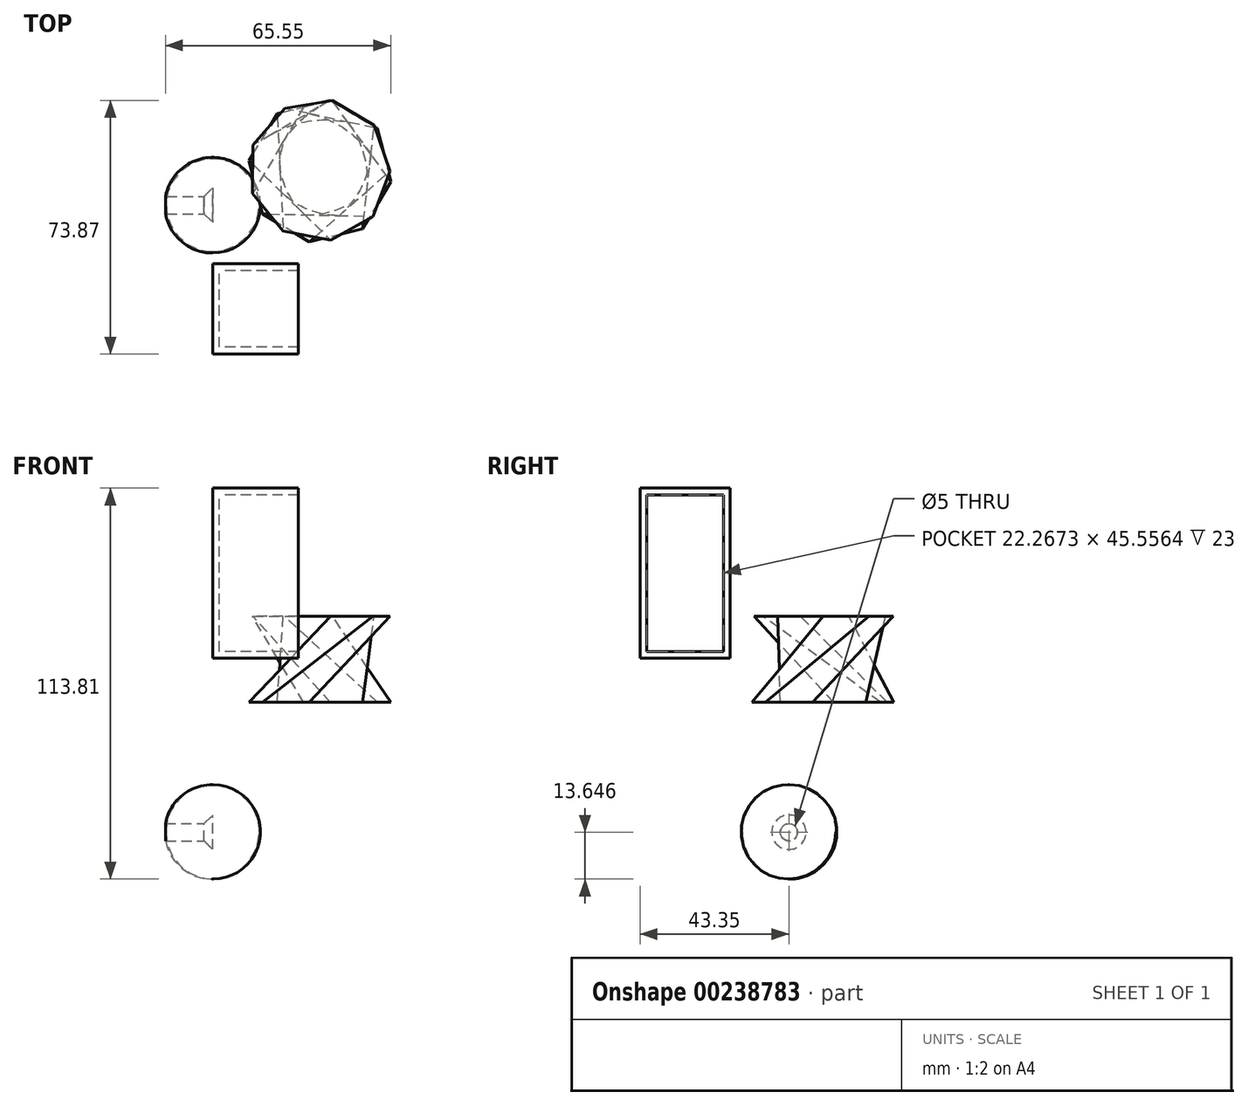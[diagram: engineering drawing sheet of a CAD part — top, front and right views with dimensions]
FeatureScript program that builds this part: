
annotation { "Feature Type Name" : "Feature", "Feature Type Description" : "" }
export const myFeature = defineFeature(function(context is Context, id is Id, definition is map)
    precondition{}
    {
        {
            var Q0;
            Q0=qCreatedBy(makeId("Top.planeOp"),FACE);
            cPlane(context, id + "F0", {"entities" : qUnion([Q0]), "cplaneType" : CPlaneType.OFFSET, "offset" : 25 * mm, "width" : 150 * mm, "height" : 150 * mm});
        }
        {
            var Q0;
            Q0=qCreatedBy(makeId("Top.planeOp"),FACE);
            var sketch = newSketch(context, id + "F1", { "sketchPlane" : qUnion([Q0])});
            skCircle(sketch, "E0.cCircle", {"center": v(31.22, 9.9) * mm, "radius": 19.26 * mm, "construction": true});
            skLineSegment(sketch, "E0.0", {"start": v(51.84, 6.85) * mm, "end": v(43.65, -6.85) * mm});
            skLineSegment(sketch, "E0.1", {"start": v(43.65, -6.85) * mm, "end": v(28.17, -10.73) * mm});
            skLineSegment(sketch, "E0.2", {"start": v(28.17, -10.73) * mm, "end": v(14.48, -2.54) * mm});
            skLineSegment(sketch, "E0.3", {"start": v(14.48, -2.54) * mm, "end": v(10.6, 12.94) * mm});
            skLineSegment(sketch, "E0.4", {"start": v(10.6, 12.94) * mm, "end": v(18.8, 26.63) * mm});
            skLineSegment(sketch, "E0.5", {"start": v(18.8, 26.63) * mm, "end": v(34.27, 30.52) * mm});
            skLineSegment(sketch, "E0.6", {"start": v(34.27, 30.52) * mm, "end": v(47.96, 22.32) * mm});
            skLineSegment(sketch, "E0.7", {"start": v(47.96, 22.32) * mm, "end": v(51.84, 6.85) * mm});
            skPoint(sketch, "E0.0.midPoint", {"position": v(47.75, 0) * mm});
            skSolve(sketch);
        }
        {
            var Q0;
            Q0=qCreatedBy(id+"F0.planeOp",FACE);
            var sketch = newSketch(context, id + "F2", { "sketchPlane" : qUnion([Q0])});
            skCircle(sketch, "E1.cCircle", {"center": v(31.04, 10.16) * mm, "radius": 20.6 * mm, "construction": true});
            skLineSegment(sketch, "E1.0", {"start": v(46.65, -3.27) * mm, "end": v(34.36, -10.16) * mm});
            skLineSegment(sketch, "E1.1", {"start": v(34.36, -10.16) * mm, "end": v(20.52, -7.54) * mm});
            skLineSegment(sketch, "E1.2", {"start": v(20.52, -7.54) * mm, "end": v(11.6, 3.36) * mm});
            skLineSegment(sketch, "E1.3", {"start": v(11.6, 3.36) * mm, "end": v(11.78, 17.45) * mm});
            skLineSegment(sketch, "E1.4", {"start": v(11.78, 17.45) * mm, "end": v(20.96, 28.13) * mm});
            skLineSegment(sketch, "E1.5", {"start": v(20.96, 28.13) * mm, "end": v(34.87, 30.4) * mm});
            skLineSegment(sketch, "E1.6", {"start": v(34.87, 30.4) * mm, "end": v(46.98, 23.2) * mm});
            skLineSegment(sketch, "E1.7", {"start": v(46.98, 23.2) * mm, "end": v(51.63, 9.9) * mm});
            skLineSegment(sketch, "E1.8", {"start": v(51.63, 9.9) * mm, "end": v(46.65, -3.27) * mm});
            skSolve(sketch);
        }
        {
            var Q0;
            Q0=makeQuery(id+"F1.imprint","IMPRINT",FACE,{"disambiguationData":[TD([[makeQuery(id+"F1.imprint","IMPRINT",EDGE,{"derivedFrom":sQuery(id+"F1.wireOp",EDGE,"E0.0")}),-1.0]])]});
            var Q1;
            Q1=makeQuery(id+"F2.imprint","IMPRINT",FACE,{"disambiguationData":[TD([[makeQuery(id+"F2.imprint","IMPRINT",EDGE,{"derivedFrom":sQuery(id+"F2.wireOp",EDGE,"E1.0")}),-1.0]])]});
            var Q2;
            Q2=sQuery(id+"F1.wireOp",VERTEX,"E0.2.start");
            var Q3;
            Q3=sQuery(id+"F2.wireOp",VERTEX,"E1.7.end");
            loft(context, id + "F3", {"sheetProfilesArray" : [{ "sheetProfileEntities" : qUnion([Q0]) }, { "sheetProfileEntities" : qUnion([Q1]) }], "matchConnections" : true, "connections" : [{ "connectionEntities" : qUnion([Q2, Q3]), "connectionEdgeQueries" : qUnion([]), "connectionEdgeParameters" : [] }]});
        }
        {
            var Q0;
            Q0=qCreatedBy(makeId("Front.planeOp"),FACE);
            var sketch = newSketch(context, id + "F4", { "sketchPlane" : qUnion([Q0])});
            skLineSegment(sketch, "E2", {"start": v(0, -17.33) * mm, "end": v(0, -59.43) * mm});
            skArc(sketch, "E3", {"start": v(0, -51.47) * mm, "mid": v(13.93, -37.73) * mm, "end": v(0, -24) * mm});
            skSolve(sketch);
        }
        {
            var Q0;
            {var subQ0=sQuery(id+"F4.wireOp",EDGE,"E3");Q0=makeQuery(id+"F4.imprint","IMPRINT",FACE,{"disambiguationData":[TD([[makeQuery(id+"F4.imprint","IMPRINT",EDGE,{"derivedFrom":subQ0}),1.0]])]});}
            var Q1;
            Q1=sQuery(id+"F4.wireOp",EDGE,"E2");
            revolve(context, id + "F5", {"entities" : qUnion([Q0]), "axis" : qUnion([Q1]), "revolveType" : RevolveType.FULL});
        }
        {
            var Q0;
            Q0=qCreatedBy(makeId("Right.planeOp"),FACE);
            var sketch = newSketch(context, id + "F6", { "sketchPlane" : qUnion([Q0])});
            skCircle(sketch, "E4", {"center": v(0, -37.82) * mm, "radius": 3.23 * mm});
            skSolve(sketch);
        }
        {
            var Q0;
            Q0=sQuery(id+"F6.wireOp",VERTEX,"E4.center");
            var Q1;
            Q1=makeQuery(id+"F5.opRevolve","SWEPT_BODY",BODY,{"disambiguationData":[OSD([sQuery(id+"F4.wireOp",EDGE,"E2"),sQuery(id+"F4.wireOp",EDGE,"E3")])]});
            hole(context, id + "F7", {"style" : HoleStyle.C_SINK, "endStyle" : HoleEndStyle.THROUGH, "holeDiameter" : 5 * mm, "cSinkDiameter" : 10 * mm, "cSinkAngle" : 90 * degree, "locations" : qUnion([Q0]), "scope" : qUnion([Q1]), "isTappedThrough" : true});
        }
        {
            var Q0;
            Q0=qCreatedBy(makeId("Right.planeOp"),FACE);
            var sketch = newSketch(context, id + "F8", { "sketchPlane" : qUnion([Q0])});
            skLineSegment(sketch, "E5.bottom", {"start": v(-43.35, 12.79) * mm, "end": v(-17.08, 12.79) * mm});
            skLineSegment(sketch, "E5.top", {"start": v(-43.35, 62.34) * mm, "end": v(-17.08, 62.34) * mm});
            skLineSegment(sketch, "E5.left", {"start": v(-43.35, 12.79) * mm, "end": v(-43.35, 62.34) * mm});
            skLineSegment(sketch, "E5.right", {"start": v(-17.08, 12.79) * mm, "end": v(-17.08, 62.34) * mm});
            skSolve(sketch);
        }
        {
            var Q0;
            Q0=makeQuery(id+"F8.imprint","IMPRINT",FACE,{"disambiguationData":[TD([[makeQuery(id+"F8.imprint","IMPRINT",EDGE,{"derivedFrom":sQuery(id+"F8.wireOp",EDGE,"E5.bottom")}),1.0]])]});
            extrude(context, id + "F9", {"entities" : qUnion([Q0]), "depth" : 25 * mm});
        }
        {
            var Q0;
            Q0=makeQuery(id+"F9.opExtrude","CAP_FACE",FACE,{"disambiguationData":[OSD([sQuery(id+"F8.wireOp",EDGE,"E5.bottom"),sQuery(id+"F8.wireOp",EDGE,"E5.top"),sQuery(id+"F8.wireOp",EDGE,"E5.left"),sQuery(id+"F8.wireOp",EDGE,"E5.right")])],"isStart":false});
            shell(context, id + "F10", {"entities" : qUnion([Q0]), "thickness" : 2 * mm});
        }
        {
            var Q0;
            Q0=qCreatedBy(makeId("Right.planeOp"),FACE);
            cPlane(context, id + "F11", {"entities" : qUnion([Q0]), "cplaneType" : CPlaneType.OFFSET, "offset" : 25 * mm, "width" : 150 * mm, "height" : 150 * mm});
        }
        {
            var Q0;
            Q0=qCreatedBy(id+"F11.planeOp",FACE);
            var sketch = newSketch(context, id + "F12", { "sketchPlane" : qUnion([Q0])});
            skLineSegment(sketch, "E6.0", {"start": v(-19.08, 14.79) * mm, "end": v(-19.08, 60.34) * mm});
            skLineSegment(sketch, "E7.0", {"start": v(-41.35, 60.34) * mm, "end": v(-19.08, 60.34) * mm});
            skLineSegment(sketch, "E8.0", {"start": v(-41.35, 14.79) * mm, "end": v(-41.35, 60.34) * mm});
            skLineSegment(sketch, "E9.0", {"start": v(-41.35, 14.79) * mm, "end": v(-19.08, 14.79) * mm});
            skFitSpline(sketch, "E10", {"points": [v(-19.08, 60.34) * mm, v(-28.49, 46.33) * mm, v(-41.35, 44.06) * mm, v(-41.35, 43.97) * mm], "startDerivative": vector(-11.4, -33.67) * mm, "endDerivative": vector(1.33, -2.53) * mm});
            skFitSpline(sketch, "E11", {"points": [v(-41.35, 14.79) * mm, v(-30.03, 25.82) * mm, v(-19.08, 28.09) * mm, v(-19.08, 28) * mm], "startDerivative": vector(17.24, 24.95) * mm, "endDerivative": vector(-1.19, -2.47) * mm});
            skSolve(sketch);
        }
        {
            var Q0;
            Q0=sQuery(id+"F12.wireOp",EDGE,"E10");
            var Q1;
            Q1=makeQuery(id+"F10.opShell","OFFSET_FACE",FACE,{"disambiguationData":[OSD([sQuery(id+"F8.wireOp",EDGE,"E5.bottom"),sQuery(id+"F8.wireOp",EDGE,"E5.top"),sQuery(id+"F8.wireOp",EDGE,"E5.left"),sQuery(id+"F8.wireOp",EDGE,"E5.right")])]});
            extrude(context, id + "F13", {"bodyType" : ToolBodyType.SURFACE, "surfaceEntities" : qUnion([Q0]), "endBound" : BoundingType.UP_TO_SURFACE, "oppositeDirection" : true, "endBoundEntityFace" : qUnion([Q1]), "depth" : 25 * mm});
        }
    });
